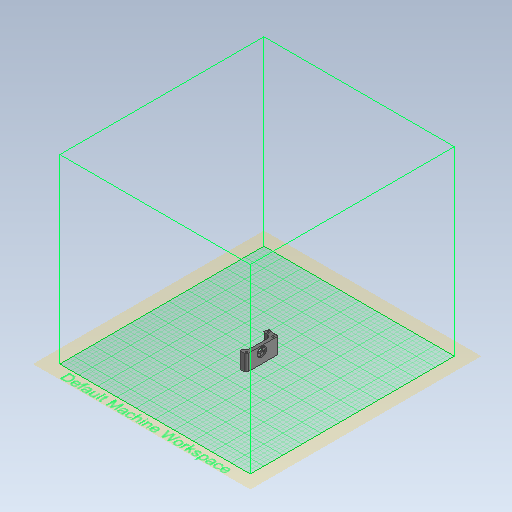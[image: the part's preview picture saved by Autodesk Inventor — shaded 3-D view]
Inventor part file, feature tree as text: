
AUTODESK INVENTOR PART (.ipt)
format: ipt  version: 2020 (Build 240168000, 168)  size: 685,568 bytes
history: native  units: mm
features: extrude x6, sketch x5, other x1, chamfer x1, fillet x1, projected_geometry x1
ambient origin geometry x8: Origin, YZ Plane, XZ Plane, XY Plane, X Axis, Y Axis, Z Axis, Center Point
bodies: Body1 (feature_tree)
feature tree (15):
  other  "Твердое тело1"
  sketch  "Эскиз1"
  extrude  "Выдавливание10"  Depth=3.8mm
  sketch  "Эскиз6"
  extrude  "Выдавливание13"  Depth=6.0mm
  extrude  "Выдавливание14"  Depth=35.0mm TaperAngle=0.0deg
  chamfer  "Фаска3"  Distance=59.0mm
  extrude  "Выдавливание15"  Depth=16.5mm
  fillet  "Сопряжение1"  Radius=10.0mm
  extrude  "Выдавливание16"  Depth=6.4mm
  extrude  "Выдавливание17"  Depth=2.3mm
  sketch  "Эскиз7"
  sketch  "Эскиз8"
  projected_geometry  "Спроецированная петля3"
  sketch  "Эскиз9"
